# Revit family: OK-Celite_Tanque 38 Litros Grande_51266
name_source: partatom
category: Plumbing Fixtures
revit_build: Autodesk Revit MEP 2014 (Build: 20131024_2115(x64)
units: mm (PartAtom-declared; Revit-internal decimal feet)

## types (2) — shared parameters
Assembly Code = D2010400
Celite: Categoria = Tanques
Celite: Código = 51266
Celite: Desenho Técnico = http://www.celite.com.br
Celite: Fabricante = Celite
Celite: Linha = Tanques
Celite: Link do Produto = http://www.celite.com.br
Celite: Norma = ABNT NBR 15097-1: 2011 - Requisitos e métodos de ensaio
Celite: Produto = Louças
Celite: Tipo = Tanques
Celite: Versão = Autodesk Revit MEP 2014
Desenvolvido por = ofcdesk
Diâmetro Ponto de Esgoto = 40 mm
Manufacturer = Celite
Model = 51266
Raio Ponto de Esgoto = 20 mm
Selo de Qualidade ofcdesk = Standard
URL = http://www.celite.com.br
WFU = 2
zero-valued in all types: CWFU, Default Elevation, HWFU

## per-type parameters (varying)
| type | Celite: Cores Disponíveis | Celite: Descrição | Description |
| Branco - 51266 | Branco | Tanque grande para capacidade de 38 litros, cor branca (51266), com coluna, linha Tanques - Louças Celite | Tanque grande para capacidade de 38 litros, cor branca (51266), com coluna, linha Tanques - Louças Celite |
| Pergamon - 51266 | Pergamon | Tanque grande para capacidade de 38 litros, cor pergamon (51266), com coluna, linha Tanques - Louças Celite | Tanque grande para capacidade de 38 litros, cor pergamon (51266), com coluna, linha Tanques - Louças Celite |

## geometry (parser evidence)
native form markers: Sweep x10
no freeform markers — native parametric forms only
